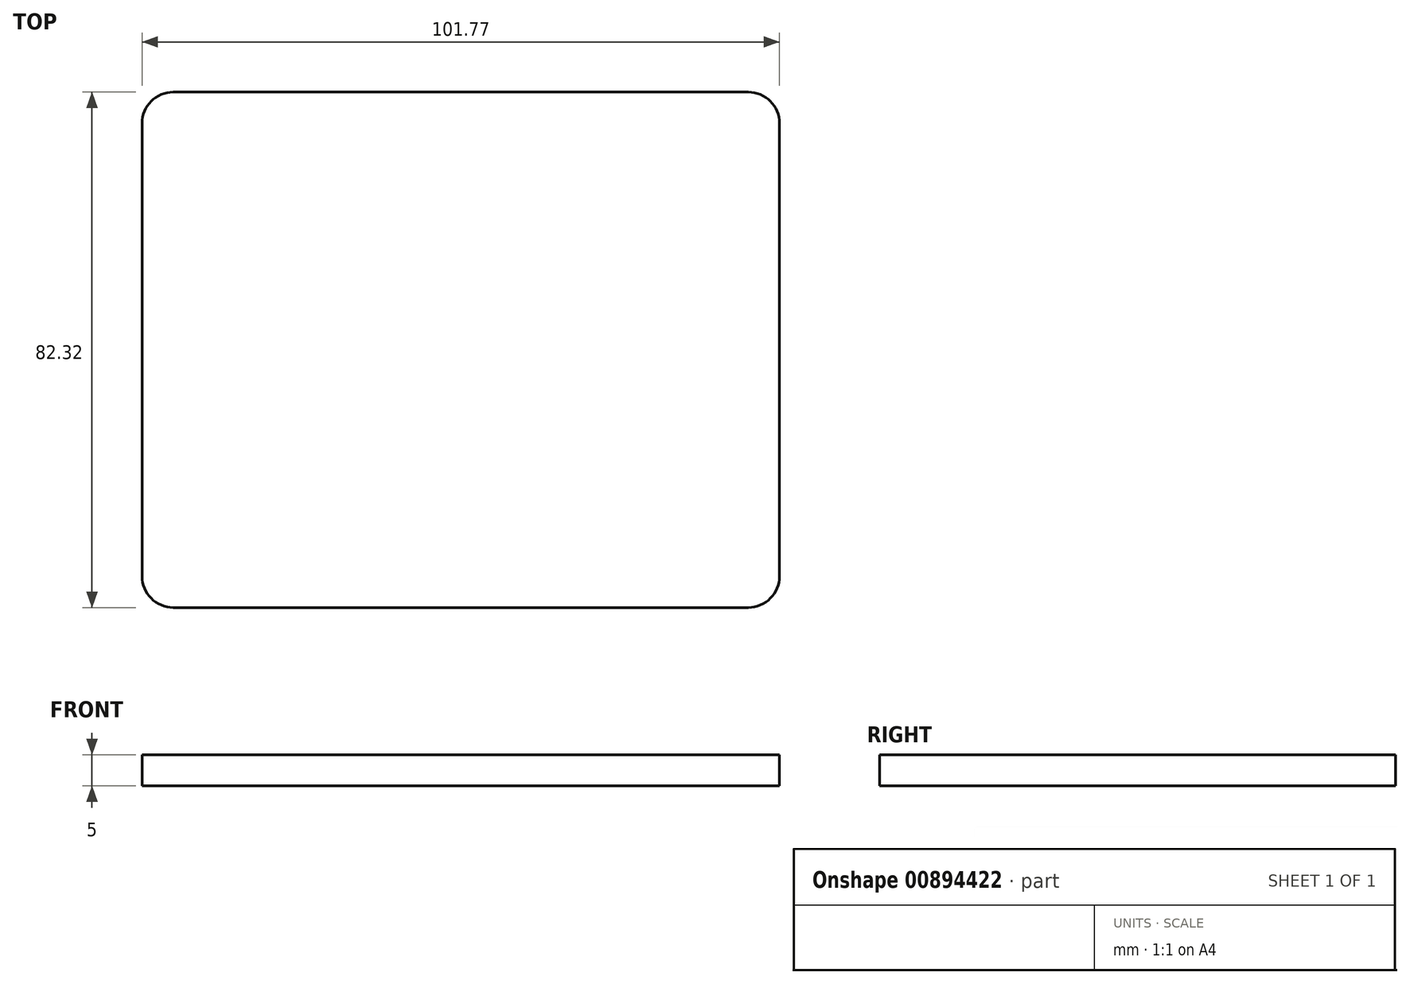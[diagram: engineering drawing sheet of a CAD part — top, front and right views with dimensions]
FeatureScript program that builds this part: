
annotation { "Feature Type Name" : "Feature", "Feature Type Description" : "" }
export const myFeature = defineFeature(function(context is Context, id is Id, definition is map)
    precondition{}
    {
        {
            var Q0;
            Q0=qCreatedBy(makeId("Top.planeOp"),FACE);
            var sketch = newSketch(context, id + "F0", { "sketchPlane" : qUnion([Q0])});
            skLineSegment(sketch, "E0.bottom", {"start": v(-36.56, 38.63) * mm, "end": v(55.2, 38.63) * mm});
            skLineSegment(sketch, "E0.top", {"start": v(-36.56, -43.7) * mm, "end": v(55.2, -43.7) * mm});
            skLineSegment(sketch, "E0.left", {"start": v(-41.56, 33.63) * mm, "end": v(-41.56, -38.7) * mm});
            skLineSegment(sketch, "E0.right", {"start": v(60.2, 33.63) * mm, "end": v(60.2, -38.7) * mm});
            skPoint(sketch, "E1.visualSharp", {"position": v(-41.56, 38.63) * mm});
            skArc(sketch, "E1.filletArc", {"start": v(-36.56, 38.63) * mm, "mid": v(-40.1, 37.16) * mm, "end": v(-41.56, 33.63) * mm});
            skPoint(sketch, "E2.visualSharp", {"position": v(60.2, 38.63) * mm});
            skArc(sketch, "E2.filletArc", {"start": v(60.2, 33.63) * mm, "mid": v(58.74, 37.16) * mm, "end": v(55.2, 38.63) * mm});
            skPoint(sketch, "E3.visualSharp", {"position": v(-41.56, -43.7) * mm});
            skArc(sketch, "E3.filletArc", {"start": v(-41.56, -38.7) * mm, "mid": v(-40.1, -42.23) * mm, "end": v(-36.56, -43.7) * mm});
            skPoint(sketch, "E4.visualSharp", {"position": v(60.2, -43.7) * mm});
            skArc(sketch, "E4.filletArc", {"start": v(55.2, -43.7) * mm, "mid": v(58.74, -42.23) * mm, "end": v(60.2, -38.7) * mm});
            skSolve(sketch);
        }
        {
            var Q0;
            Q0=makeQuery(id+"F0.imprint","IMPRINT",FACE,{"disambiguationData":[TD([[makeQuery(id+"F0.imprint","IMPRINT",EDGE,{"derivedFrom":sQuery(id+"F0.wireOp",EDGE,"E0.bottom")}),-1.0]])]});
            extrude(context, id + "F1", {"entities" : qUnion([Q0]), "depth" : 5 * mm, "offsetDistance" : 25 * mm});
        }
    });
